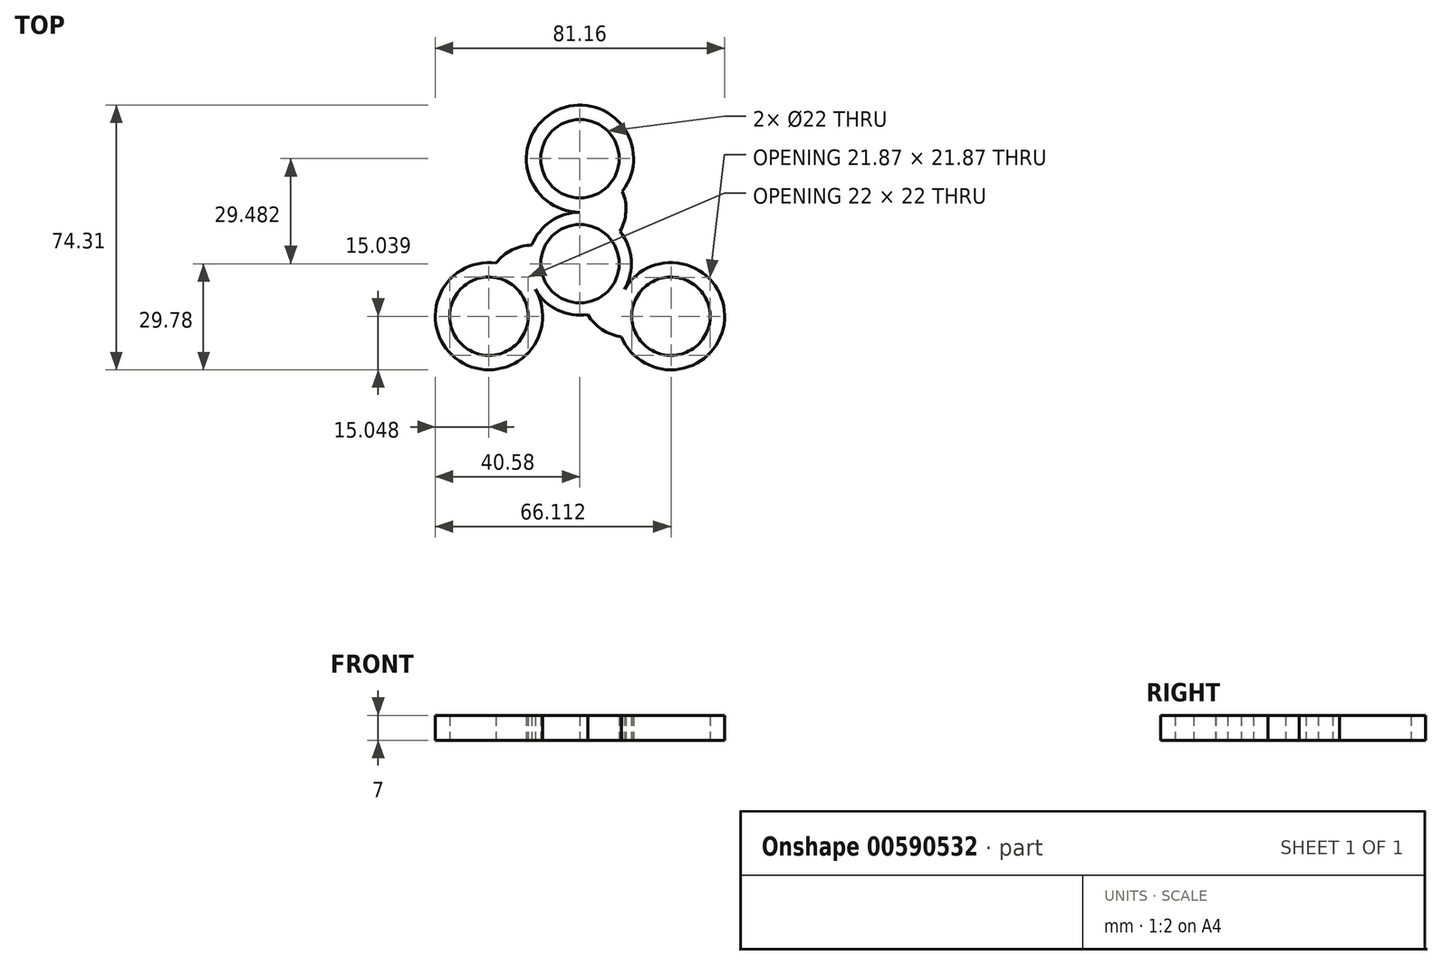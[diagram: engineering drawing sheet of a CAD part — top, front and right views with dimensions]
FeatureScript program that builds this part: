
annotation { "Feature Type Name" : "Feature", "Feature Type Description" : "" }
export const myFeature = defineFeature(function(context is Context, id is Id, definition is map)
    precondition{}
    {
        {
            var Q0;
            Q0=qCreatedBy(makeId("Top.planeOp"),FACE);
            var sketch = newSketch(context, id + "F0", { "sketchPlane" : qUnion([Q0])});
            skArc(sketch, "E0", {"start": v(-20.69, -4.87) * mm, "mid": v(-20.64, -5.07) * mm, "end": v(-20.59, -5.26) * mm});
            skCircle(sketch, "E1", {"center": v(0, 29.48) * mm, "radius": 11 * mm});
            skCircle(sketch, "E2.1.0", {"center": v(-25.53, -14.74) * mm, "radius": 11 * mm});
            skCircle(sketch, "E2.2.0", {"center": v(25.53, -14.74) * mm, "radius": 11 * mm});
            skArc(sketch, "E3", {"start": v(-13.46, 5.21) * mm, "mid": v(-19.1, 3.87) * mm, "end": v(-23.56, 0.17) * mm});
            skArc(sketch, "E4", {"start": v(-18.1, -1.66) * mm, "mid": v(-16.38, -0.62) * mm, "end": v(-14.44, -0.08) * mm});
            skArc(sketch, "E5.1.1", {"start": v(2.22, -14.27) * mm, "mid": v(6.2, -18.47) * mm, "end": v(11.63, -20.49) * mm});
            skArc(sketch, "E5.2.1", {"start": v(12.82, 16.94) * mm, "mid": v(12.5, 18.66) * mm, "end": v(11.93, 20.31) * mm});
            skArc(sketch, "E6.1.0", {"start": v(10.49, -14.85) * mm, "mid": v(8.73, -13.87) * mm, "end": v(7.29, -12.46) * mm});
            skArc(sketch, "E6.1.1", {"start": v(8.26, -19.58) * mm, "mid": v(9.91, -20.15) * mm, "end": v(11.63, -20.49) * mm});
            skArc(sketch, "E6.2.0", {"start": v(7.62, 16.5) * mm, "mid": v(7.65, 14.5) * mm, "end": v(7.15, 12.54) * mm});
            skArc(sketch, "E6.2.1", {"start": v(11.25, 9.05) * mm, "mid": v(12.9, 14.6) * mm, "end": v(11.93, 20.31) * mm});
            skArc(sketch, "E7", {"start": v(11.93, 20.31) * mm, "mid": v(-9.96, 40.76) * mm, "end": v(7.62, 16.5) * mm});
            skArc(sketch, "E8.1.0", {"start": v(-23.56, 0.17) * mm, "mid": v(-30.32, -29) * mm, "end": v(-18.1, -1.66) * mm});
            skArc(sketch, "E8.2.0", {"start": v(11.63, -20.49) * mm, "mid": v(40.28, -11.76) * mm, "end": v(10.49, -14.85) * mm});
            skPoint(sketch, "E9.orphan", {"position": v(15.94, -20.3) * mm});
            skPoint(sketch, "E10.orphan", {"position": v(14.54, -15.26) * mm});
            skArc(sketch, "E11", {"start": v(-14.44, -0.08) * mm, "mid": v(-9.36, -10.99) * mm, "end": v(2.22, -14.27) * mm});
            skPoint(sketch, "E12.orphan", {"position": v(-21.09, 2.63) * mm});
            skPoint(sketch, "E13.orphan", {"position": v(-20.59, -5.26) * mm});
            skPoint(sketch, "E14.orphan", {"position": v(-20.49, -4.97) * mm});
            skPoint(sketch, "E15.orphan", {"position": v(-25.55, -3.65) * mm});
            skArc(sketch, "E16.trimOffspring", {"start": v(7.29, -12.46) * mm, "mid": v(14.2, -2.61) * mm, "end": v(11.25, 9.05) * mm});
            skPoint(sketch, "E17.orphan", {"position": v(14.85, -15.2) * mm});
            skPoint(sketch, "E18.orphan", {"position": v(8.26, -19.58) * mm});
            skPoint(sketch, "E19.orphan", {"position": v(5.73, 20.46) * mm});
            skPoint(sketch, "E20.orphan", {"position": v(12.82, 16.94) * mm});
            skArc(sketch, "E21.trimOffspring", {"start": v(7.15, 12.54) * mm, "mid": v(-4.84, 13.6) * mm, "end": v(-13.46, 5.21) * mm});
            skPoint(sketch, "E22.orphan", {"position": v(5.94, 20.22) * mm});
            skPoint(sketch, "E23.orphan", {"position": v(9.61, 23.95) * mm});
            skArc(sketch, "E24.trimOffspring", {"start": v(14.56, -15.48) * mm, "mid": v(14.7, -15.34) * mm, "end": v(14.85, -15.2) * mm});
            skArc(sketch, "E25.trimOffspring", {"start": v(6.13, 20.35) * mm, "mid": v(5.93, 20.4) * mm, "end": v(5.73, 20.46) * mm});
            skCircle(sketch, "E26", {"center": v(0, 0) * mm, "radius": 11 * mm});
            skSolve(sketch);
        }
        {
            var Q0;
            Q0 = qSketchRegion(id + "F0", true);
            var Q1;
            Q1=makeQuery(id+"F0.imprint","IMPRINT",FACE,{"disambiguationData":[TD([[makeQuery(id+"F0.imprint","IMPRINT",EDGE,{"derivedFrom":sQuery(id+"F0.wireOp",EDGE,"E1")}),-1.0]])]});
            extrude(context, id + "F1", {"entities" : qUnion([Q0, Q1]), "depth" : 7 * mm, "offsetDistance" : 25 * mm});
        }
    });
